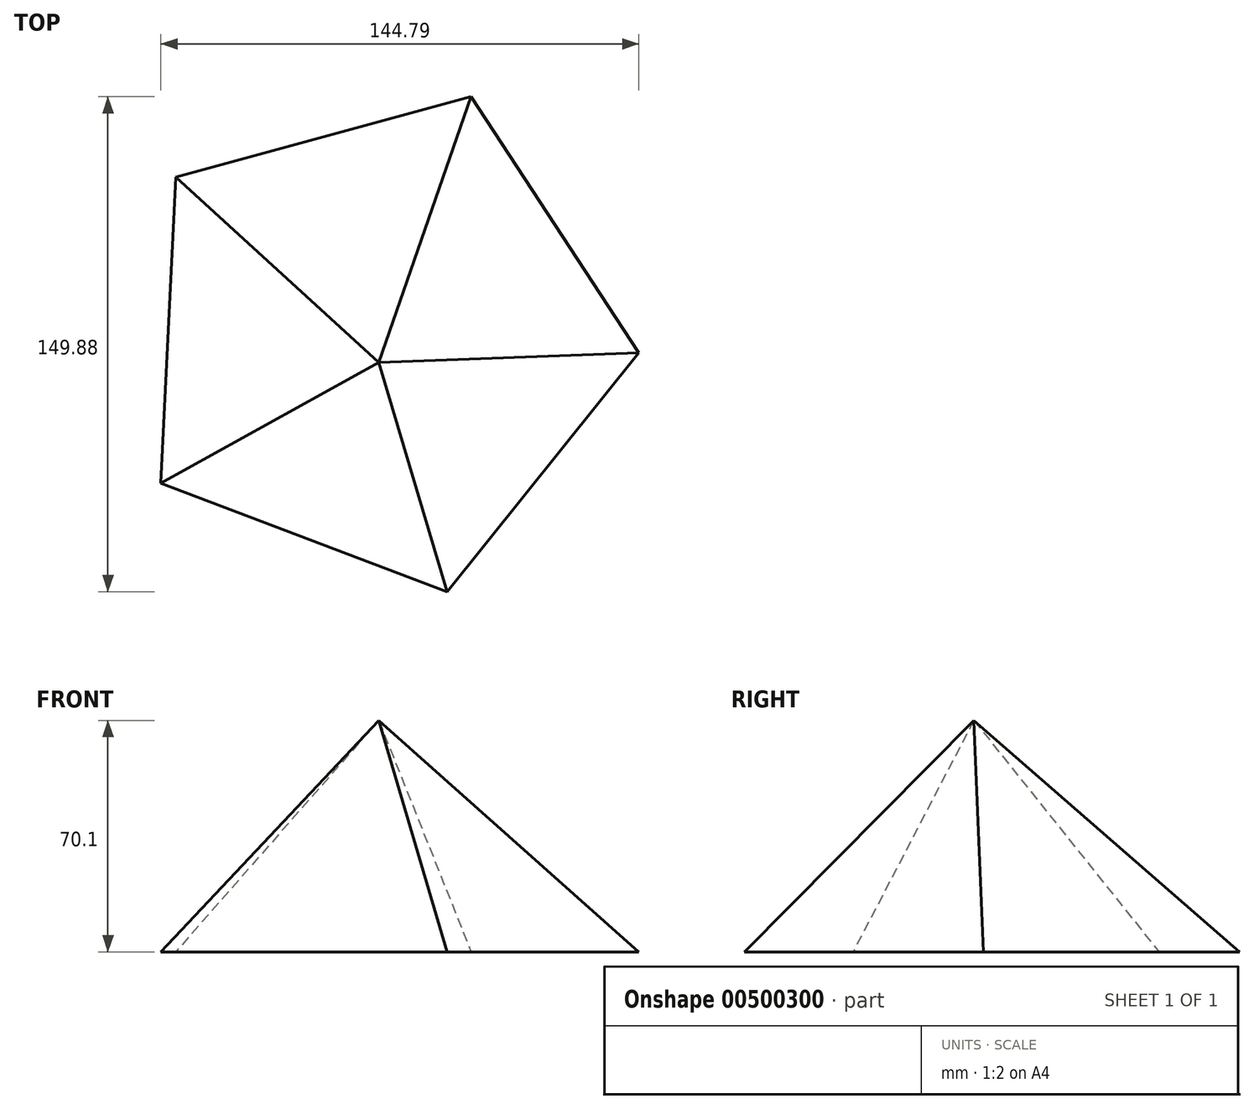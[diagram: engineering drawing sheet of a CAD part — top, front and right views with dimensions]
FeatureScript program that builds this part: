
annotation { "Feature Type Name" : "Feature", "Feature Type Description" : "" }
export const myFeature = defineFeature(function(context is Context, id is Id, definition is map)
    precondition{}
    {
        {
            var Q0;
            Q0=qCreatedBy(makeId("Top.planeOp"),FACE);
            var sketch = newSketch(context, id + "F0", { "sketchPlane" : qUnion([Q0])});
            skCircle(sketch, "E0.cCircle", {"center": v(0, 0) * mm, "radius": 78.89 * mm, "construction": true});
            skLineSegment(sketch, "E0.0", {"start": v(-61.5, 49.4) * mm, "end": v(27.98, 73.76) * mm});
            skLineSegment(sketch, "E0.1", {"start": v(27.98, 73.76) * mm, "end": v(78.8, -3.82) * mm});
            skLineSegment(sketch, "E0.2", {"start": v(78.8, -3.82) * mm, "end": v(20.72, -76.12) * mm});
            skLineSegment(sketch, "E0.3", {"start": v(20.72, -76.12) * mm, "end": v(-66, -43.22) * mm});
            skLineSegment(sketch, "E0.4", {"start": v(-66, -43.22) * mm, "end": v(-61.5, 49.4) * mm});
            skSolve(sketch);
        }
        {
            var Q0;
            Q0=qCreatedBy(makeId("Top.planeOp"),FACE);
            cPlane(context, id + "F1", {"entities" : qUnion([Q0]), "cplaneType" : CPlaneType.OFFSET, "offset" : 70.1 * mm, "width" : 152.4 * mm, "height" : 152.4 * mm});
        }
        {
            var Q0;
            Q0=qCreatedBy(id+"F1.planeOp",FACE);
            var sketch = newSketch(context, id + "F2", { "sketchPlane" : qUnion([Q0])});
            skPoint(sketch, "E1", {"position": v(0, -6.68) * mm});
            skSolve(sketch);
        }
        {
            var Q0;
            Q0=sQuery(id+"F2.wireOp",VERTEX,"E1");
            var Q1;
            Q1=makeQuery(id+"F0.imprint","IMPRINT",FACE,{"disambiguationData":[TD([[makeQuery(id+"F0.imprint","IMPRINT",EDGE,{"derivedFrom":sQuery(id+"F0.wireOp",EDGE,"E0.0")}),-1.0]])]});
            loft(context, id + "F3", {"sheetProfilesArray" : [{ "sheetProfileEntities" : qUnion([Q0]) }, { "sheetProfileEntities" : qUnion([Q1]) }]});
        }
    });
